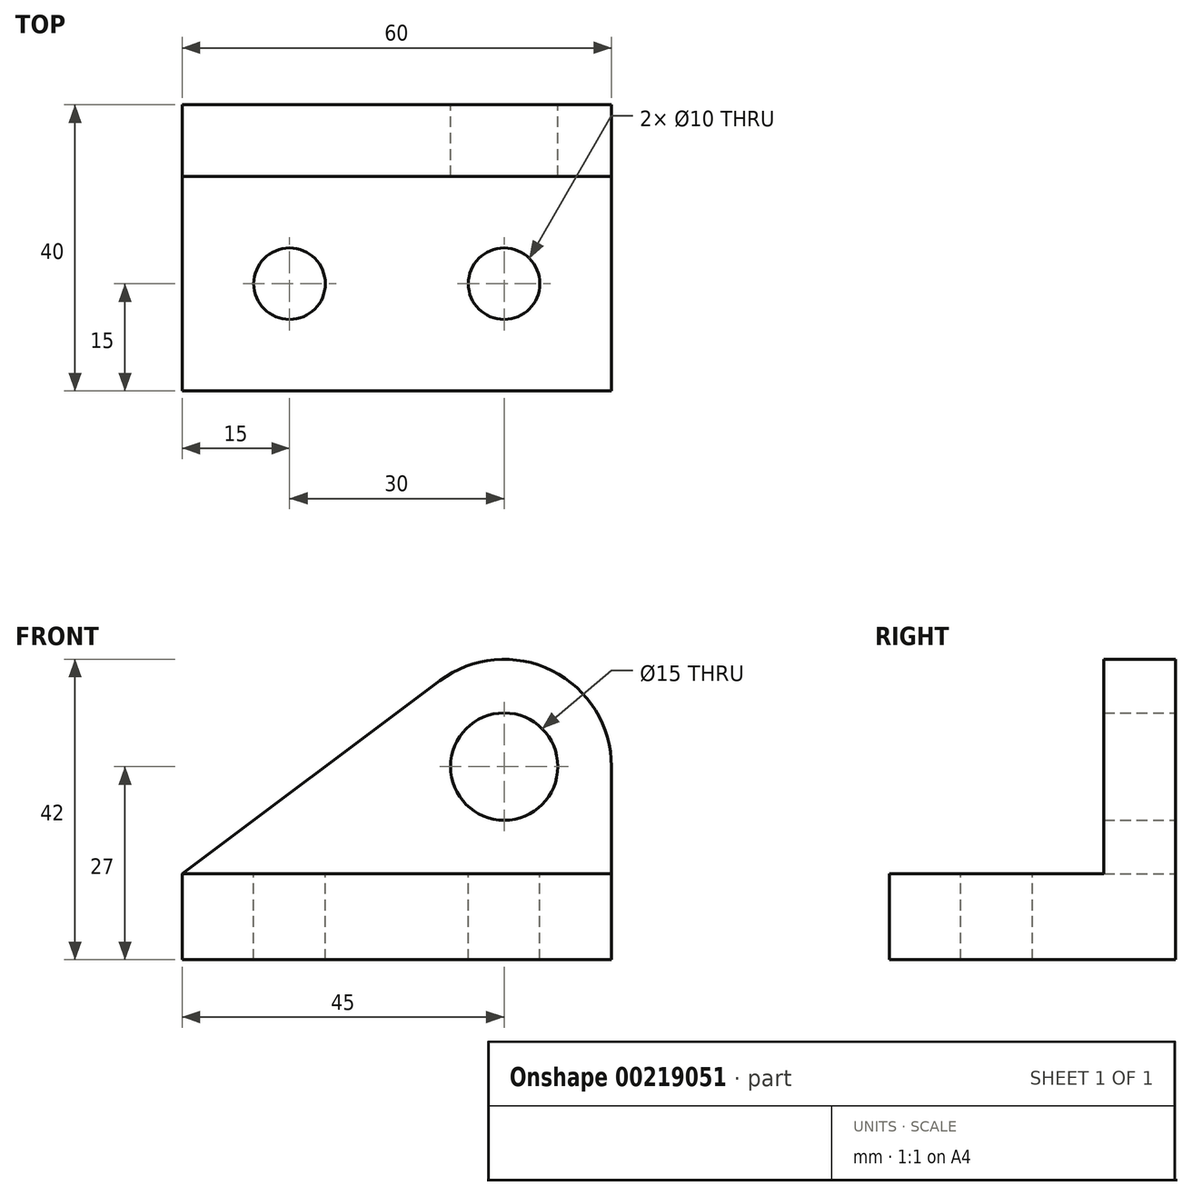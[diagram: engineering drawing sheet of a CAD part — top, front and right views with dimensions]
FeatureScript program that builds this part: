
annotation { "Feature Type Name" : "Feature", "Feature Type Description" : "" }
export const myFeature = defineFeature(function(context is Context, id is Id, definition is map)
    precondition{}
    {
        {
            var Q0;
            Q0=qCreatedBy(makeId("Front.planeOp"),FACE);
            var sketch = newSketch(context, id + "F0", { "sketchPlane" : qUnion([Q0])});
            skLineSegment(sketch, "E0", {"start": v(0, 0) * mm, "end": v(60, 0) * mm});
            skLineSegment(sketch, "E1", {"start": v(60, 0) * mm, "end": v(60, 12) * mm});
            skLineSegment(sketch, "E2", {"start": v(60, 12) * mm, "end": v(0, 12) * mm});
            skLineSegment(sketch, "E3", {"start": v(0, 12) * mm, "end": v(0, 0) * mm});
            skCircle(sketch, "E4", {"center": v(45, 27) * mm, "radius": 7.5 * mm});
            skArc(sketch, "E5", {"start": v(60, 27) * mm, "mid": v(51.7, 40.42) * mm, "end": v(36, 39) * mm});
            skLineSegment(sketch, "E6", {"start": v(60, 27) * mm, "end": v(60, 12) * mm});
            skLineSegment(sketch, "E7", {"start": v(0, 12) * mm, "end": v(36, 39) * mm});
            skSolve(sketch);
        }
        {
            var Q0;
            Q0=makeQuery(id+"F0.imprint","IMPRINT",FACE,{"disambiguationData":[TD([[makeQuery(id+"F0.imprint","IMPRINT",EDGE,{"derivedFrom":sQuery(id+"F0.wireOp",EDGE,"E0")}),1.0]])]});
            extrude(context, id + "F1", {"entities" : qUnion([Q0]), "depth" : 40 * mm});
        }
        {
            var Q0;
            Q0=makeQuery(id+"F0.imprint","IMPRINT",FACE,{"disambiguationData":[TD([[makeQuery(id+"F0.imprint","IMPRINT",EDGE,{"derivedFrom":sQuery(id+"F0.wireOp",EDGE,"E2")}),-1.0]])]});
            extrude(context, id + "F2", {"entities" : qUnion([Q0]), "operationType" : NewBodyOperationType.ADD, "depth" : 10 * mm});
        }
        {
            var Q0;
            Q0=makeQuery(id+"F1.opExtrude","SWEPT_FACE",FACE,{"disambiguationData":[OSD([sQuery(id+"F0.wireOp",EDGE,"E2")])]});
            var sketch = newSketch(context, id + "F3", { "sketchPlane" : qUnion([Q0])});
            skCircle(sketch, "E8", {"center": v(15, -25) * mm, "radius": 5 * mm});
            skCircle(sketch, "E9", {"center": v(45, -25) * mm, "radius": 5 * mm});
            skSolve(sketch);
        }
        {
            var Q0;
            Q0 = qSketchRegion(id + "F3", true);
            extrude(context, id + "F4", {"entities" : qUnion([Q0]), "operationType" : NewBodyOperationType.REMOVE, "endBound" : BoundingType.UP_TO_NEXT, "oppositeDirection" : true, "depth" : 25 * mm});
        }
    });
